# Revit family: Indirect-Water-Heater_AO_Smith-IT-3000_N
name_source: partatom
category: Mechanical Equipment
revit_build: Autodesk Revit 2016 (Build: 20170117_1200(x64)
units: mm (PartAtom-declared; Revit-internal decimal feet)

## family parameters
Always vertical = Yes
Cut with Voids When Loaded = No
OmniClass Number = 23.75.00.00
OmniClass Title = Climate Control (HVAC)
Part Type = Normal
Room Calculation Point = No
Round Connector Dimension = Use Radius
Shared = No
Work Plane-Based = No

## types (1)
- IT 3000 N
    1e Maintenance (check-up) = 3 maanden na installatie
    2nd Maintenance (general maintenance) = 12 maanden na installatie
    Assembly Code = D3010
    BIM Content Developer = CAD & Company
    BIM Content Developer URL = http://www.cadcompany.nl
    Category = Mechanical Equipment
    Cold Water Connection R = 2"
    Description = Indirecte Boiler met 1 warmtewisselaar
    Destination / Counrty = Nederland
    Diameter (with insulation) = 1600 mm  [stored 5.24934 ft]
    Diameter (without insulation) = 1400 mm  [stored 4.59318 ft]
    Draw-off Capacity @ ΔT = 28°C after 120 min. = 10699.0 L
    Draw-off Capacity @ ΔT = 28°C after 30 min. = 4018.0 L
    Draw-off Capacity @ ΔT = 28°C after 60 min. = 6245.0 L
    Draw-off Capacity @ ΔT = 28°C after 90 min. = 8472.0 L
    Draw-off Capacity @ ΔT = 44°C after 120 min. = 6808.0 L
    Draw-off Capacity @ ΔT = 44°C after 30 min. = 2557.0 L
    Draw-off Capacity @ ΔT = 44°C after 60 min. = 3974.0 L
    Draw-off Capacity @ ΔT = 44°C after 90 min. = 5391.0 L
    Draw-off Capacity @ ΔT = 50°C after 120 min. = 5991.0 L
    Draw-off Capacity @ ΔT = 50°C after 30 min. = 2250.0 L
    Draw-off Capacity @ ΔT = 50°C after 60 min. = 3497.0 L
    Draw-off Capacity @ ΔT = 50°C after 90 min. = 4744.0 L
    Draw-off Capacity @ ΔT = 55°C after 120 min. = 5447.0 L
    Draw-off Capacity @ ΔT = 55°C after 30 min. = 2046.0 L
    Draw-off Capacity @ ΔT = 55°C after 60 min. = 3179.0 L
    Draw-off Capacity @ ΔT = 55°C after 90 min. = 4313.0 L
    Draw-off Capacity @ ΔT = 70°C after 120 min. = 4279.0 L
    Draw-off Capacity @ ΔT = 70°C after 30 min. = 1607.0 L
    Draw-off Capacity @ ΔT = 70°C after 60 min. = 2498.0 L
    Draw-off Capacity @ ΔT = 70°C after 90 min. = 3389.0 L
    Empty Weight = 600.00 kg
    Flow Rate - Volume L/h = 6871
    Heating Up Time @ ΔT = 28°C = 14
    Heating Up Time @ ΔT = 44°C = 21
    Heating Up Time @ ΔT = 50°C = 24
    Heating Up Time @ ΔT = 55°C = 27
    Heating Up Time @ ΔT = 70°C = 34
    Height (with insulation) = 2045 mm  [stored 6.70932 ft]
    Height (without insulation) = 2045 mm  [stored 6.70932 ft]
    Height Cold Water Inlet = 185 mm  [stored 0.606955 ft]
    Height Warm Water Outlet = 2045 mm  [stored 6.70932 ft]
    Host = Unhosted
    Hot / Warm Water Connection R = 2"
    Insulation Thickness = 100 mm  [stored 0.328084 ft]
    Maintenance Interval = 12 maanden
    Manufacturer = A.O. Smith Water Products Company b.v.
    Manufacturer Number = E 7110
E 7110
E 7110
    Max. Operating Pressure - bottom heat exchanger = 600000.0 Pa
    Max. Operating Pressure - tank = 80000.0 Pa
    Max. Tempature - bottom heat exchanger = 90 °C
    Max. Temperature - tank = 85 °C
    Model = IT 3000 N
    NLSfB = 51.11
    Nominal Output - bottom heat exchanger = 156000 W
    Operating Weight = 3400.00 kg
    Packaging Height = 2195 mm  [stored 7.20144 ft]
    Packaging Length = 1680 mm  [stored 5.51181 ft]
    Packaging Width = 1498 mm  [stored 4.9147 ft]
    Pressure Loss - bottom heat exchanger 80ºC/60ºC = 695000.0 Pa
    Product Documentation Link = https://www.aosmithinternational.com
    Product Instruction Link = https://www.aosmithinternational.com
    Productcode = 8717449172763
    Productversion = 1.0
    Recovery Rate @ ΔT = 28°C (ltr/hr) = 4454
    Recovery Rate @ ΔT = 44°C (ltr/hr) = 2834
    Recovery Rate @ ΔT = 50°C (ltr/hr) = 2494
    Recovery Rate @ ΔT = 55°C (ltr/hr) = 2267
    Recovery Rate @ ΔT = 70°C (ltr/hr) = 1781
    Serial Number = 8717449172763
    Stand-by Loss = 0 W
    Stand-by Loss - daily (Watt/24H) = 0
    Storage Capacity - bottom heat exchanger = 45 m³
    Storage Capacity - tank = 2800 m³
    Surface bottom heat Exchanger = 6 m²
    T&P Connection Rp = 1"
    Transport Weight = 720.00 kg
    Type of Packaging = Plastic en Hout
    URL = www.aosmith.nl
    Warranty on Parts = 12 maanden
    Warranty on Tank = 36 maanden
    Workspace Diameter = 2600 mm  [stored 8.53018 ft]
    Workspace Height = 3045 mm

note: [stored X ft] marks values corroborated as IEEE doubles in the binary element streams (Revit-internal decimal feet)

## geometry (parser evidence)
native form markers: Blend x2, Sweep x20
no freeform markers — native parametric forms only
